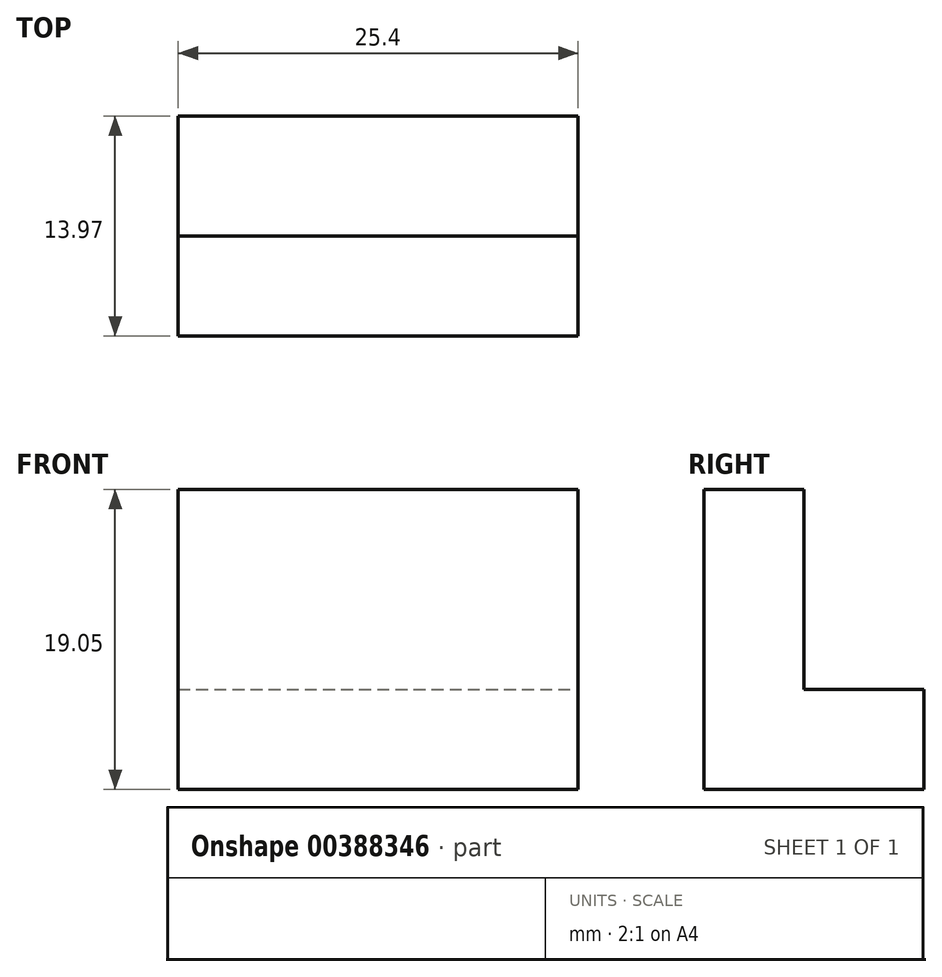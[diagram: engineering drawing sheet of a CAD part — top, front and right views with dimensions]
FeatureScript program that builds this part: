
annotation { "Feature Type Name" : "Feature", "Feature Type Description" : "" }
export const myFeature = defineFeature(function(context is Context, id is Id, definition is map)
    precondition{}
    {
        {
            var Q0;
            Q0=qCreatedBy(makeId("Front.planeOp"),FACE);
            var sketch = newSketch(context, id + "F0", { "sketchPlane" : qUnion([Q0])});
            skLineSegment(sketch, "E0.bottom", {"start": v(0, 0) * mm, "end": v(25.4, 0) * mm});
            skLineSegment(sketch, "E0.top", {"start": v(0, 19.05) * mm, "end": v(25.4, 19.05) * mm});
            skLineSegment(sketch, "E0.left", {"start": v(0, 0) * mm, "end": v(0, 19.05) * mm});
            skLineSegment(sketch, "E0.right", {"start": v(25.4, 0) * mm, "end": v(25.4, 19.05) * mm});
            skSolve(sketch);
        }
        {
            var Q0;
            Q0 = qSketchRegion(id + "F0", true);
            extrude(context, id + "F1", {"entities" : qUnion([Q0]), "depth" : 6.35 * mm});
        }
        {
            var Q0;
            Q0=makeQuery(id+"F1.opExtrude","CAP_FACE",FACE,{"disambiguationData":[OSD([sQuery(id+"F0.wireOp",EDGE,"E0.bottom"),sQuery(id+"F0.wireOp",EDGE,"E0.top"),sQuery(id+"F0.wireOp",EDGE,"E0.left"),sQuery(id+"F0.wireOp",EDGE,"E0.right")])],"isStart":true});
            var sketch = newSketch(context, id + "F2", { "sketchPlane" : qUnion([Q0])});
            skLineSegment(sketch, "E1.bottom", {"start": v(0, 0) * mm, "end": v(-25.4, 0) * mm});
            skLineSegment(sketch, "E1.top", {"start": v(0, 6.35) * mm, "end": v(-25.4, 6.35) * mm});
            skLineSegment(sketch, "E1.left", {"start": v(0, 0) * mm, "end": v(0, 6.35) * mm});
            skLineSegment(sketch, "E1.right", {"start": v(-25.4, 0) * mm, "end": v(-25.4, 6.35) * mm});
            skSolve(sketch);
        }
        {
            var Q0;
            Q0=makeQuery(id+"F2.imprint","IMPRINT",FACE,{"disambiguationData":[TD([[makeQuery(id+"F2.imprint","IMPRINT",EDGE,{"derivedFrom":sQuery(id+"F2.wireOp",EDGE,"E1.bottom")}),-1.0]])]});
            extrude(context, id + "F3", {"entities" : qUnion([Q0]), "operationType" : NewBodyOperationType.ADD, "depth" : 7.62 * mm});
        }
    });
